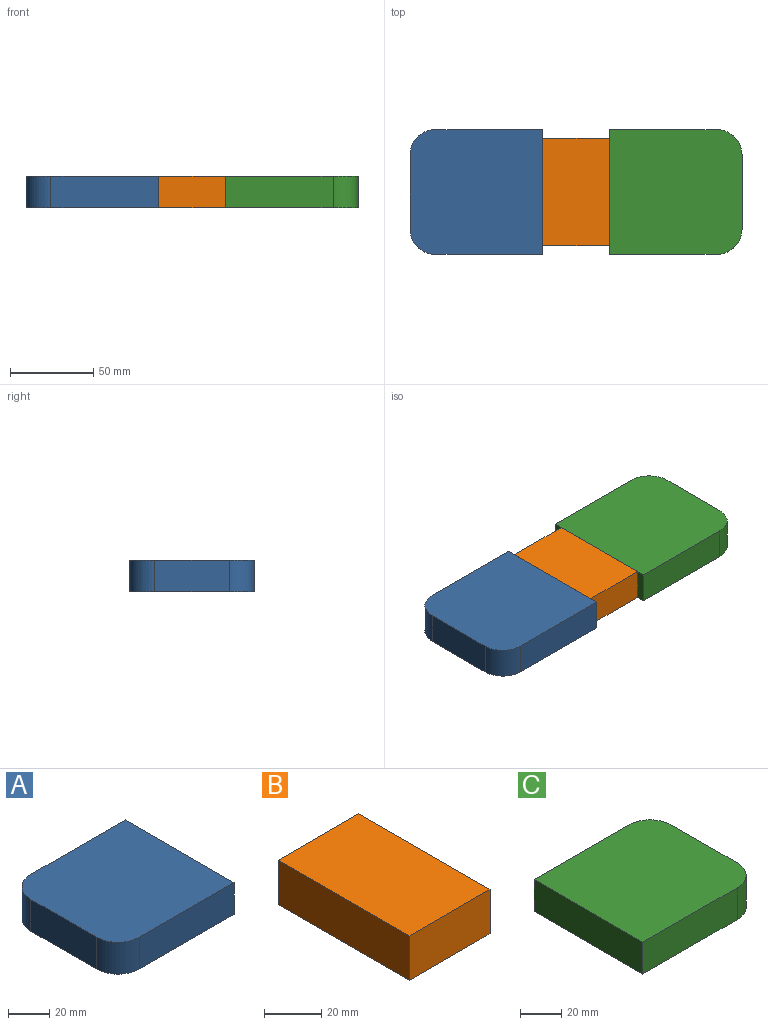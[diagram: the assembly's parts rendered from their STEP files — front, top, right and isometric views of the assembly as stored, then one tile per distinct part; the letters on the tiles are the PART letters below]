
ASSEMBLY  parts=3 mates=6
PART A: 8 faces, bbox 80x75x19 mm
  f0: cylinder r=15mm len=19mm, axis (0,0,-1), area 447.7mm2, adj f1,f5,f6,f7
  f1: plane 65x19mm, normal (0,-1,0), area 1235mm2, adj f0,f2,f6,f7
  f2: plane 75x19mm, normal (1,0,0), area 1425mm2, adj f1,f3,f6,f7
  f3: plane 65x19mm, normal (0,1,0), area 1235mm2, adj f2,f4,f6,f7
  f4: cylinder r=15mm len=19mm, axis (0,0,-1), area 447.7mm2, adj f3,f5,f6,f7
  f5: plane 45x19mm, normal (-1,0,0), area 855mm2, adj f0,f4,f6,f7
  f6: plane 80x75mm, normal (0,0,1), area 5903.4mm2, adj f0,f1,f2,f3,f4,f5
  f7: plane 80x75mm, normal (0,0,-1), area 5903.4mm2, adj f0,f1,f2,f3,f4,f5
PART B: 6 faces, bbox 40x65x19 mm
  f0: plane 65x19mm, normal (-1,0,0), area 1235mm2, adj f1,f3,f4,f5
  f1: plane 40x19mm, normal (0,-1,0), area 760mm2, adj f0,f2,f4,f5
  f2: plane 65x19mm, normal (1,0,0), area 1235mm2, adj f1,f3,f4,f5
  f3: plane 40x19mm, normal (0,1,0), area 760mm2, adj f0,f2,f4,f5
  f4: plane 65x40mm, normal (0,0,1), area 2600mm2, adj f0,f1,f2,f3
  f5: plane 65x40mm, normal (0,0,-1), area 2600mm2, adj f0,f1,f2,f3
PART C: 8 faces, bbox 80x75x19 mm
  f0: plane 65x19mm, normal (0,1,0), area 1235mm2, adj f1,f5,f6,f7
  f1: plane 75x19mm, normal (-1,0,0), area 1425mm2, adj f0,f2,f6,f7
  f2: plane 65x19mm, normal (0,-1,0), area 1235mm2, adj f1,f3,f6,f7
  f3: cylinder r=15mm len=19mm, axis (0,0,-1), area 447.7mm2, adj f2,f4,f6,f7
  f4: plane 45x19mm, normal (1,0,0), area 855mm2, adj f3,f5,f6,f7
  f5: cylinder r=15mm len=19mm, axis (0,0,-1), area 447.7mm2, adj f0,f4,f6,f7
  f6: plane 80x75mm, normal (0,0,1), area 5903.4mm2, adj f0,f1,f2,f3,f4,f5
  f7: plane 80x75mm, normal (0,0,-1), area 5903.4mm2, adj f0,f1,f2,f3,f4,f5
PLACE A t=(199.24,94.2,-40.39)mm
PLACE B t=(27.56,99.2,-40.39)mm
PLACE C t=(192.26,94.2,-40.39)mm
MATE parallel B.f2 <-> C.f1  axis (1,0,0) through (134.48,71.5,-30.89)mm
MATE parallel A.f2 <-> B.f0  axis (1,0,0) through (94.48,71.5,-30.89)mm
MATE parallel A.f2 <-> B.f0  axis (1,0,0) through (94.48,71.5,-30.89)mm
MATE parallel B.f2 <-> C.f1  axis (1,0,0) through (134.48,71.5,-30.89)mm
MATE parallel B.f0 <-> A.f2  axis (-1,0,0) through (94.48,71.5,-30.89)mm
MATE parallel C.f1 <-> B.f2  axis (-1,0,0) through (134.48,71.5,-30.89)mm
